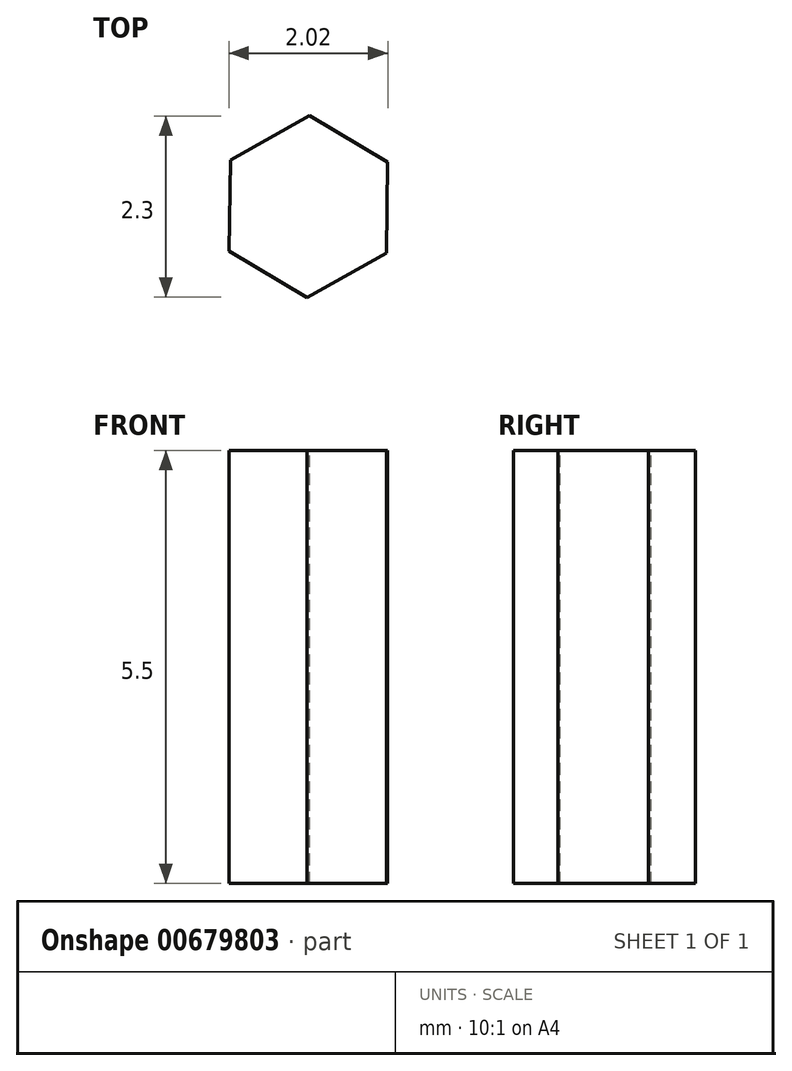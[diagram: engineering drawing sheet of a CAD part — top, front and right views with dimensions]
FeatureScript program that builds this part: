
annotation { "Feature Type Name" : "Feature", "Feature Type Description" : "" }
export const myFeature = defineFeature(function(context is Context, id is Id, definition is map)
    precondition{}
    {
        {
            var Q0;
            Q0=qCreatedBy(makeId("Top.planeOp"),FACE);
            var sketch = newSketch(context, id + "F0", { "sketchPlane" : qUnion([Q0])});
            skCircle(sketch, "E0", {"center": v(0, 0) * mm, "radius": 2.5 * mm});
            skSolve(sketch);
        }
        {
            var Q0;
            Q0=sQuery(id+"F0.wireOp",EDGE,"E0");
            extrude(context, id + "F1", {"bodyType" : ToolBodyType.SURFACE, "surfaceEntities" : qUnion([Q0]), "depth" : 25 * mm, "offsetDistance" : 25 * mm});
        }
        {
            var Q0;
            Q0=qCreatedBy(makeId("Top.planeOp"),FACE);
            var sketch = newSketch(context, id + "F2", { "sketchPlane" : qUnion([Q0])});
            skCircle(sketch, "E1.cCircle", {"center": v(0, 0) * mm, "radius": 1 * mm, "construction": true});
            skLineSegment(sketch, "E1.0", {"start": v(0.02, 1.15) * mm, "end": v(1, 0.56) * mm});
            skLineSegment(sketch, "E1.1", {"start": v(1, 0.56) * mm, "end": v(1, -0.6) * mm});
            skLineSegment(sketch, "E1.2", {"start": v(1, -0.6) * mm, "end": v(-0.02, -1.15) * mm});
            skLineSegment(sketch, "E1.3", {"start": v(-0.02, -1.15) * mm, "end": v(-1, -0.56) * mm});
            skLineSegment(sketch, "E1.4", {"start": v(-1, -0.56) * mm, "end": v(-1, 0.6) * mm});
            skLineSegment(sketch, "E1.5", {"start": v(-1, 0.6) * mm, "end": v(0.02, 1.15) * mm});
            skPoint(sketch, "E1.0.midPoint", {"position": v(0.51, 0.86) * mm});
            skSolve(sketch);
        }
        {
            var Q0;
            Q0=makeQuery(id+"F2.imprint","IMPRINT",FACE,{"disambiguationData":[TD([[makeQuery(id+"F2.imprint","IMPRINT",EDGE,{"derivedFrom":sQuery(id+"F2.wireOp",EDGE,"E1.0")}),-1.0]])]});
            var Q1;
            Q1=makeQuery(id+"F1.opExtrude","SWEPT_FACE",FACE,{"disambiguationData":[OSD([sQuery(id+"F0.wireOp",EDGE,"E0")])]});
            extrude(context, id + "F3", {"entities" : qUnion([Q0]), "oppositeDirection" : true, "depth" : 5.5 * mm, "endBoundEntityFace" : qUnion([Q1]), "offsetDistance" : 25 * mm});
        }
    });
